# Revit family: Csmt-1
name_source: partatom
category: Windows
revit_build: Autodesk Revit Architecture 2013 (Build: 20121003_2115(x64)
units: mm (PartAtom-declared; Revit-internal decimal feet)

## types (4) — shared parameters
Analytic Construction = <None>
Apron Overlap = 0"
Default Head Height = 8' - 0"
Frame - Interior = Wood
Head Overlap = 0"
Mas. Header/Sill = Masonry - Brick Soldier Course
Muntin Depth = 5/8"
Muntin Width = 3/4"
Trim - Exterior = Andersen(R) - White
Trim - Head Height = 5 1/2"
Trim - Interior = Wood
Trim - Side Width = 5 1/2"
Wall Closure = By host
Window Inset = 1"

## per-type parameters (varying)
| type | Apron Thickness | Default Sill Height | Frame - Exterior | Glass Height | Glass Width | Height | Model | Sash | Sash Height | Trim - Apron Height | Width | Window Grille |
| 2-0 x 4-0 | 3/4" | 4' - 0" | Andersen(R) - White | 3' - 7" | 1' - 7" | 4' - 0" | 2040 CSMT | Andersen(R) - White | 2' - 0" | 5 1/2" | 2' - 0" | Andersen(R) - White |
| 2-0 x 3-0 | 1 1/2" | 5' - 0" | Matte Black | 2' - 7" | 1' - 7" | 3' - 0" | 2030 CSMT | Matte Black | 1' - 6" | 2" | 2' - 0" | Matte Black |
| 2-0 x 5-0 | 1 1/2" | 3' - 0" | Matte Black | 4' - 7" | 1' - 7" | 5' - 0" | 2050 CSMT | Matte Black | 2' - 6" | 2" | 2' - 0" | Matte Black |
| 5-0 x 1-6 | 1 1/2" | 6' - 6" | Matte Black | 1' - 1" | 4' - 7" | 1' - 6" |  | Matte Black | 9" | 2" | 5' - 0" | Matte Black |

## geometry (parser evidence)
native form markers: Blend x4, Sweep x3
no freeform markers — native parametric forms only
